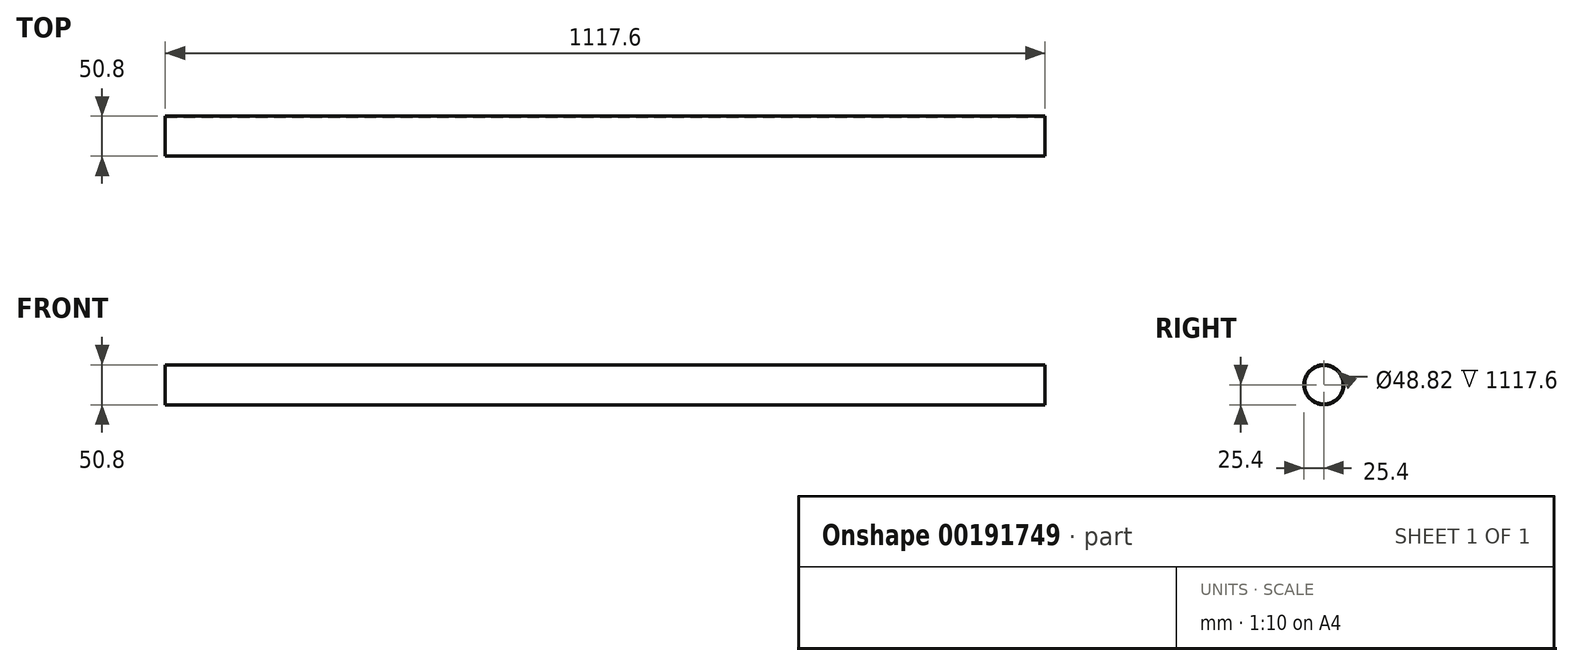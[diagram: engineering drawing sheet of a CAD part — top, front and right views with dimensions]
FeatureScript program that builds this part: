
annotation { "Feature Type Name" : "Feature", "Feature Type Description" : "" }
export const myFeature = defineFeature(function(context is Context, id is Id, definition is map)
    precondition{}
    {
        {
            var Q0;
            Q0=qCreatedBy(makeId("Right.planeOp"),FACE);
            var sketch = newSketch(context, id + "F0", { "sketchPlane" : qUnion([Q0])});
            skCircle(sketch, "E0", {"center": v(0, 0) * mm, "radius": 25.4 * mm});
            skSolve(sketch);
        }
        {
            var Q0;
            Q0=makeQuery(id+"F0.imprint","IMPRINT",FACE,{"disambiguationData":[TD([[makeQuery(id+"F0.imprint","IMPRINT",EDGE,{"derivedFrom":sQuery(id+"F0.wireOp",EDGE,"E0")}),1.0]])]});
            extrude(context, id + "F1", {"entities" : qUnion([Q0]), "depth" : 1117.6 * mm});
        }
        {
            var Q0;
            Q0=makeQuery(id+"F1.opExtrude","CAP_FACE",FACE,{"disambiguationData":[OSD([sQuery(id+"F0.wireOp",EDGE,"E0")])],"isStart":false});
            var sketch = newSketch(context, id + "F2", { "sketchPlane" : qUnion([Q0])});
            skCircle(sketch, "E1", {"center": v(0, 0) * mm, "radius": 24.4 * mm});
            skSolve(sketch);
        }
        {
            var Q0;
            Q0=makeQuery(id+"F2.imprint","IMPRINT",FACE,{"disambiguationData":[TD([[makeQuery(id+"F2.imprint","IMPRINT",EDGE,{"derivedFrom":sQuery(id+"F2.wireOp",EDGE,"E1")}),1.0]])]});
            var Q1;
            Q1=makeQuery(id+"F1.opExtrude","CAP_FACE",FACE,{"disambiguationData":[OSD([sQuery(id+"F0.wireOp",EDGE,"E0")])],"isStart":true});
            extrude(context, id + "F3", {"entities" : qUnion([Q0, Q1]), "operationType" : NewBodyOperationType.REMOVE, "oppositeDirection" : true, "depth" : 1120.14 * mm});
        }
    });
